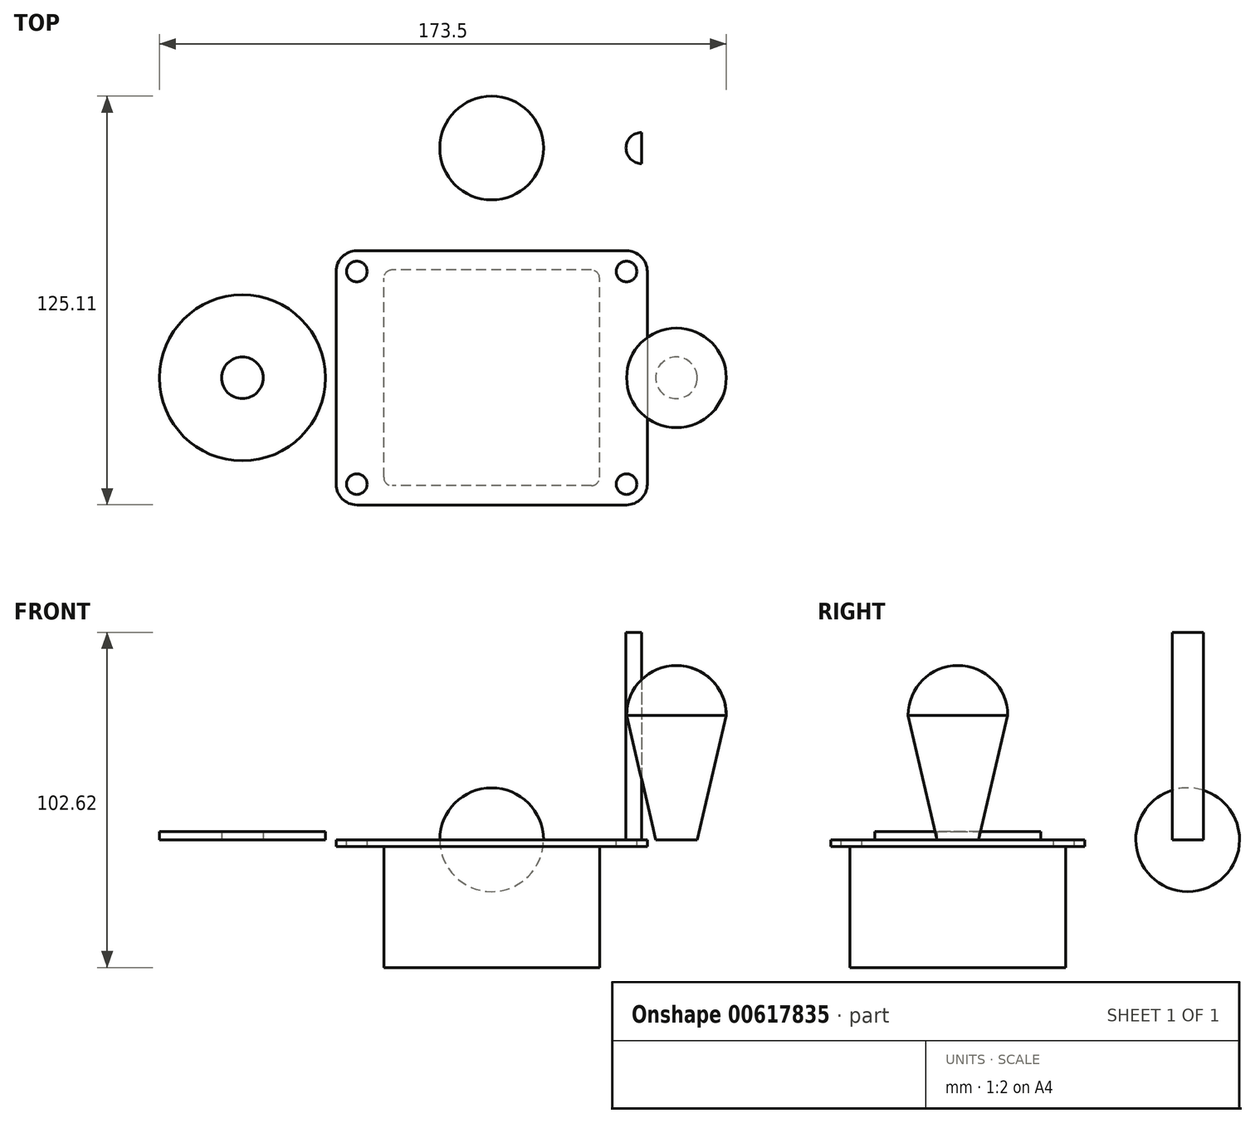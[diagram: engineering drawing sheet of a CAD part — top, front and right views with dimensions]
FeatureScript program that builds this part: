
annotation { "Feature Type Name" : "Feature", "Feature Type Description" : "" }
export const myFeature = defineFeature(function(context is Context, id is Id, definition is map)
    precondition{}
    {
        {
            var Q0;
            Q0=qCreatedBy(makeId("Top.planeOp"),FACE);
            var sketch = newSketch(context, id + "F0", { "sketchPlane" : qUnion([Q0])});
            skLineSegment(sketch, "E0.bottom", {"start": v(41.28, 38.9) * mm, "end": v(-41.28, 38.9) * mm});
            skLineSegment(sketch, "E0.top", {"start": v(41.28, -38.9) * mm, "end": v(-41.28, -38.9) * mm});
            skLineSegment(sketch, "E0.left", {"start": v(47.63, 32.54) * mm, "end": v(47.63, -32.54) * mm});
            skLineSegment(sketch, "E0.right", {"start": v(-47.63, 32.54) * mm, "end": v(-47.63, -32.54) * mm});
            skPoint(sketch, "E0.middle", {"position": v(0, 0) * mm});
            skPoint(sketch, "E1.visualSharp", {"position": v(-47.63, 38.9) * mm});
            skArc(sketch, "E1.filletArc", {"start": v(-41.28, 38.9) * mm, "mid": v(-45.77, 37.03) * mm, "end": v(-47.63, 32.54) * mm});
            skPoint(sketch, "E2.visualSharp", {"position": v(-47.63, -38.9) * mm});
            skArc(sketch, "E2.filletArc", {"start": v(-47.63, -32.54) * mm, "mid": v(-45.77, -37.03) * mm, "end": v(-41.28, -38.9) * mm});
            skPoint(sketch, "E3.visualSharp", {"position": v(47.63, -38.9) * mm});
            skArc(sketch, "E3.filletArc", {"start": v(41.28, -38.9) * mm, "mid": v(45.77, -37.03) * mm, "end": v(47.63, -32.54) * mm});
            skPoint(sketch, "E4.visualSharp", {"position": v(47.63, 38.9) * mm});
            skArc(sketch, "E4.filletArc", {"start": v(47.63, 32.54) * mm, "mid": v(45.77, 37.03) * mm, "end": v(41.28, 38.9) * mm});
            skCircle(sketch, "E5", {"center": v(-41.28, 32.54) * mm, "radius": 3.18 * mm});
            skCircle(sketch, "E6", {"center": v(-41.28, -32.54) * mm, "radius": 3.18 * mm});
            skCircle(sketch, "E7", {"center": v(41.28, -32.54) * mm, "radius": 3.18 * mm});
            skCircle(sketch, "E8", {"center": v(41.28, 32.54) * mm, "radius": 3.18 * mm});
            skCircle(sketch, "E9", {"center": v(0, 0) * mm, "radius": 4.76 * mm});
            skCircle(sketch, "E10", {"center": v(-76.3, 0) * mm, "radius": 25.4 * mm});
            skCircle(sketch, "E11", {"center": v(-76.3, 0) * mm, "radius": 6.35 * mm});
            skSolve(sketch);
        }
        {
            var Q0;
            Q0=makeQuery(id+"F0.imprint","IMPRINT",FACE,{"disambiguationData":[TD([[makeQuery(id+"F0.imprint","IMPRINT",EDGE,{"derivedFrom":sQuery(id+"F0.wireOp",EDGE,"E0.bottom")}),1.0]])]});
            var Q1;
            Q1=makeQuery(id+"F0.imprint","IMPRINT",FACE,{"disambiguationData":[TD([[makeQuery(id+"F0.imprint","IMPRINT",EDGE,{"derivedFrom":sQuery(id+"F0.wireOp",EDGE,"E9")}),1.0]])]});
            extrude(context, id + "F1", {"entities" : qUnion([Q0, Q1]), "oppositeDirection" : true, "depth" : 2.03 * mm, "offsetDistance" : 25.4 * mm});
        }
        {
            var Q0;
            Q0=makeQuery(id+"F1.opExtrude","CAP_FACE",FACE,{"disambiguationData":[OSD([sQuery(id+"F0.wireOp",EDGE,"E0.bottom"),sQuery(id+"F0.wireOp",EDGE,"E0.top"),sQuery(id+"F0.wireOp",EDGE,"E0.left"),sQuery(id+"F0.wireOp",EDGE,"E0.right"),sQuery(id+"F0.wireOp",EDGE,"E1.filletArc"),sQuery(id+"F0.wireOp",EDGE,"E2.filletArc"),sQuery(id+"F0.wireOp",EDGE,"E3.filletArc"),sQuery(id+"F0.wireOp",EDGE,"E4.filletArc"),sQuery(id+"F0.wireOp",EDGE,"E5"),sQuery(id+"F0.wireOp",EDGE,"E6"),sQuery(id+"F0.wireOp",EDGE,"E7"),sQuery(id+"F0.wireOp",EDGE,"E8")])],"isStart":false});
            var sketch = newSketch(context, id + "F2", { "sketchPlane" : qUnion([Q0])});
            skLineSegment(sketch, "E12.bottom", {"start": v(30.48, 33.02) * mm, "end": v(-30.48, 33.02) * mm});
            skLineSegment(sketch, "E12.top", {"start": v(30.48, -33.02) * mm, "end": v(-30.48, -33.02) * mm});
            skLineSegment(sketch, "E12.left", {"start": v(33.02, 30.48) * mm, "end": v(33.02, -30.48) * mm});
            skLineSegment(sketch, "E12.right", {"start": v(-33.02, 30.48) * mm, "end": v(-33.02, -30.48) * mm});
            skPoint(sketch, "E12.middle", {"position": v(0, 0) * mm});
            skPoint(sketch, "E13.visualSharp", {"position": v(-33.02, 33.02) * mm});
            skArc(sketch, "E13.filletArc", {"start": v(-30.48, 33.02) * mm, "mid": v(-32.28, 32.28) * mm, "end": v(-33.02, 30.48) * mm});
            skPoint(sketch, "E14.visualSharp", {"position": v(-33.02, -33.02) * mm});
            skArc(sketch, "E14.filletArc", {"start": v(-33.02, -30.48) * mm, "mid": v(-32.28, -32.28) * mm, "end": v(-30.48, -33.02) * mm});
            skPoint(sketch, "E15.visualSharp", {"position": v(33.02, -33.02) * mm});
            skArc(sketch, "E15.filletArc", {"start": v(30.48, -33.02) * mm, "mid": v(32.28, -32.28) * mm, "end": v(33.02, -30.48) * mm});
            skPoint(sketch, "E16.visualSharp", {"position": v(33.02, 33.02) * mm});
            skArc(sketch, "E16.filletArc", {"start": v(33.02, 30.48) * mm, "mid": v(32.28, 32.28) * mm, "end": v(30.48, 33.02) * mm});
            skSolve(sketch);
        }
        {
            var Q0;
            Q0=makeQuery(id+"F2.imprint","IMPRINT",FACE,{"disambiguationData":[TD([[makeQuery(id+"F2.imprint","IMPRINT",EDGE,{"derivedFrom":sQuery(id+"F2.wireOp",EDGE,"E12.bottom")}),1.0]])]});
            extrude(context, id + "F3", {"entities" : qUnion([Q0]), "operationType" : NewBodyOperationType.ADD, "depth" : 37.08 * mm, "offsetDistance" : 25.4 * mm});
        }
        {
            var Q0;
            Q0=qCreatedBy(makeId("Top.planeOp"),FACE);
            var sketch = newSketch(context, id + "F4", { "sketchPlane" : qUnion([Q0])});
            skCircle(sketch, "E17", {"center": v(0, 70.34) * mm, "radius": 15.88 * mm});
            skLineSegment(sketch, "E18", {"start": v(0, 54.47) * mm, "end": v(0, 86.22) * mm});
            skCircle(sketch, "E19", {"center": v(45.89, 70.34) * mm, "radius": 4.76 * mm});
            skArc(sketch, "E20", {"start": v(45.89, 65.58) * mm, "mid": v(50.65, 70.34) * mm, "end": v(45.89, 75.1) * mm});
            skLineSegment(sketch, "E21", {"start": v(45.89, 75.1) * mm, "end": v(45.89, 65.58) * mm});
            skSolve(sketch);
        }
        {
            var Q0;
            {var subQ0=sQuery(id+"F4.wireOp",EDGE,"E18");var subQ1=sQuery(id+"F4.wireOp",EDGE,"E17");var subQ2=makeQuery(id+"F4.imprint","INTERSECT",VERTEX,{"disambiguationData":[OD(0.0)],"derivedFrom":[subQ1,subQ0]});Q0=makeQuery(id+"F4.imprint","IMPRINT",FACE,{"disambiguationData":[TD([[makeQuery(id+"F4.imprint","IMPRINT",EDGE,{"disambiguationData":[TD([[subQ2,-1.0]])],"derivedFrom":subQ1}),1.0]])]});}
            var Q1;
            {var subQ0=sQuery(id+"F4.wireOp",EDGE,"cLlEl8t9-G464-SyIN-0L6k-VLgWYFZ1Ioiw");var subQ1=sQuery(id+"F4.wireOp",EDGE,"E18");var subQ2=makeQuery(id+"F4.imprint","INTERSECT",VERTEX,{"disambiguationData":[OD(0.0)],"derivedFrom":[subQ1,subQ0]});Q1=makeQuery(id+"F4.imprint","IMPRINT",FACE,{"disambiguationData":[TD([[makeQuery(id+"F4.imprint","IMPRINT",EDGE,{"disambiguationData":[TD([[subQ2,-1.0]])],"derivedFrom":subQ1}),-1.0]])]});}
            var Q2;
            Q2=sQuery(id+"F4.wireOp",EDGE,"E18");
            revolve(context, id + "F5", {"entities" : qUnion([Q0, Q1]), "axis" : qUnion([Q2]), "revolveType" : RevolveType.FULL});
        }
        {
            var Q0;
            Q0=qCreatedBy(makeId("Front.planeOp"),FACE);
            var sketch = newSketch(context, id + "F6", { "sketchPlane" : qUnion([Q0])});
            skLineSegment(sketch, "E22", {"start": v(56.57, 0) * mm, "end": v(56.57, 38.1) * mm});
            skLineSegment(sketch, "E23", {"start": v(56.57, 38.1) * mm, "end": v(71.8, 38.1) * mm});
            skLineSegment(sketch, "E24", {"start": v(71.8, 38.1) * mm, "end": v(62.92, 0) * mm});
            skLineSegment(sketch, "E25", {"start": v(62.92, 0) * mm, "end": v(56.57, 0) * mm});
            skArc(sketch, "E26", {"start": v(71.8, 38.1) * mm, "mid": v(67.34, 48.88) * mm, "end": v(56.57, 53.34) * mm});
            skLineSegment(sketch, "E27", {"start": v(56.57, 53.34) * mm, "end": v(56.57, 38.1) * mm});
            skSolve(sketch);
        }
        {
            var Q0;
            Q0 = qSketchRegion(id + "F6", true);
            var Q1;
            Q1=sQuery(id+"F6.wireOp",EDGE,"E22");
            revolve(context, id + "F7", {"entities" : qUnion([Q0]), "axis" : qUnion([Q1]), "revolveType" : RevolveType.FULL});
        }
        {
            var Q0;
            Q0=makeQuery(id+"F4.imprint","IMPRINT",FACE,{"disambiguationData":[TD([[makeQuery(id+"F4.imprint","IMPRINT",EDGE,{"derivedFrom":sQuery(id+"F4.wireOp",EDGE,"XLwnjqze-HLU6-kZrp-5h6E-EuwZQ5UlDlWi")}),1.0]])]});
            var Q1;
            Q1=makeQuery(id+"F4.imprint","IMPRINT",FACE,{"disambiguationData":[TD([[makeQuery(id+"F4.imprint","IMPRINT",EDGE,{"derivedFrom":sQuery(id+"F4.wireOp",EDGE,"E19")}),1.0]])]});
            extrude(context, id + "F8", {"entities" : qUnion([Q0, Q1]), "depth" : 63.5 * mm, "offsetDistance" : 25.4 * mm});
        }
        {
            var Q0;
            Q0=makeQuery(id+"F0.imprint","IMPRINT",FACE,{"disambiguationData":[TD([[makeQuery(id+"F0.imprint","IMPRINT",EDGE,{"derivedFrom":sQuery(id+"F0.wireOp",EDGE,"E10")}),1.0]])]});
            extrude(context, id + "F9", {"entities" : qUnion([Q0]), "depth" : 2.54 * mm, "offsetDistance" : 25.4 * mm});
        }
    });
